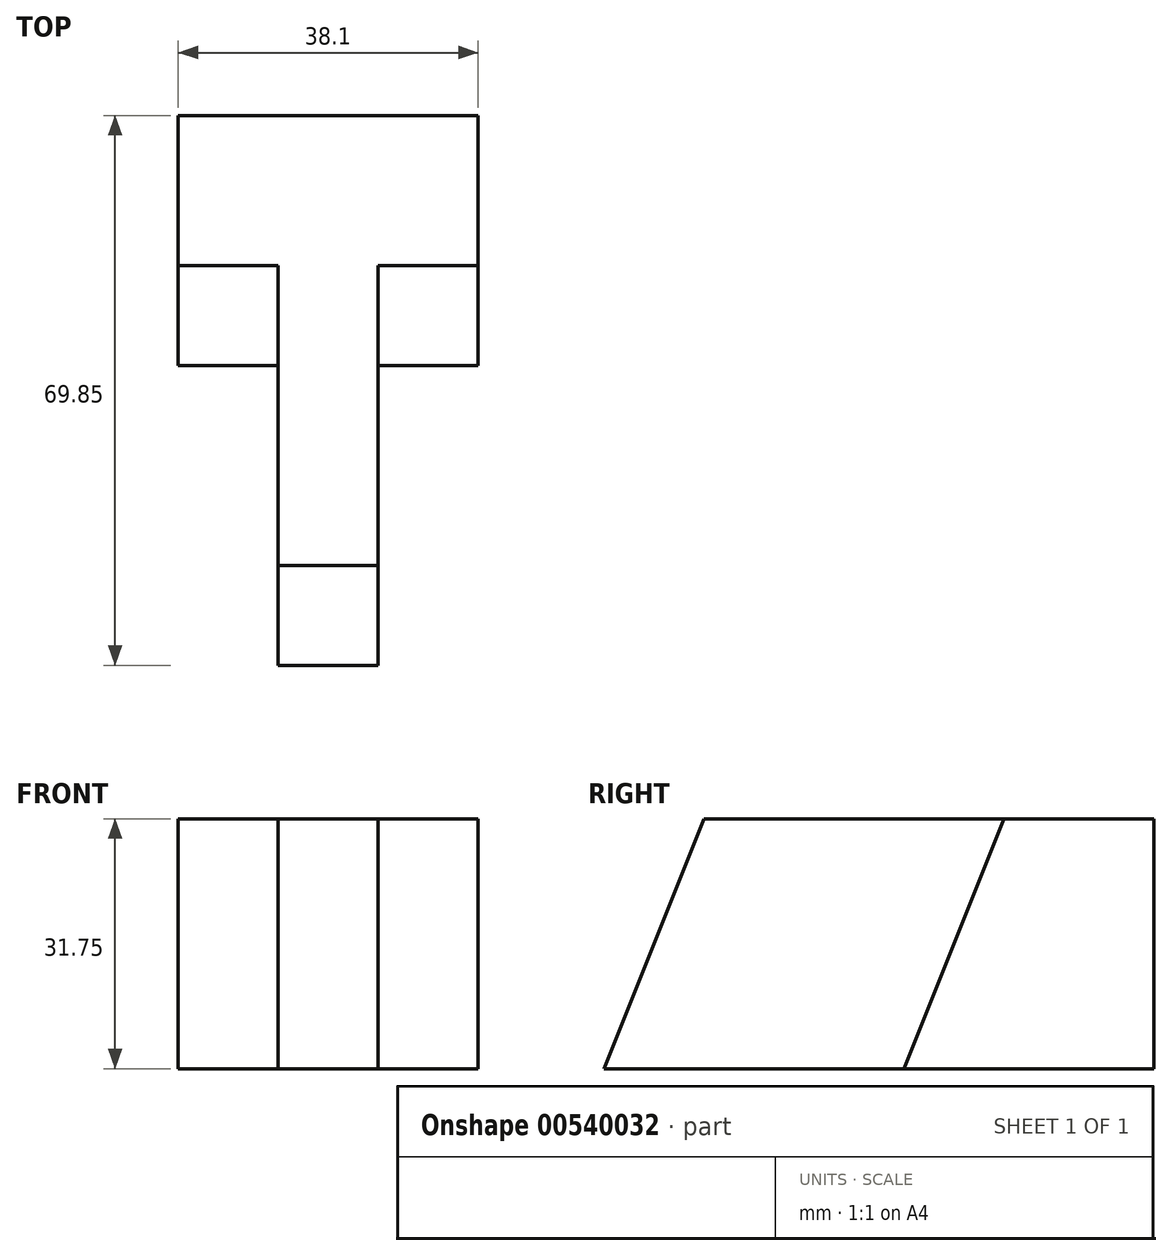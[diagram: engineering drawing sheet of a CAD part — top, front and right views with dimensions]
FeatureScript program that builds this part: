
annotation { "Feature Type Name" : "Feature", "Feature Type Description" : "" }
export const myFeature = defineFeature(function(context is Context, id is Id, definition is map)
    precondition{}
    {
        {
            var Q0;
            Q0=qCreatedBy(makeId("Top.planeOp"),FACE);
            var sketch = newSketch(context, id + "F0", { "sketchPlane" : qUnion([Q0])});
            skLineSegment(sketch, "E0", {"start": v(-15.79, 47.95) * mm, "end": v(22.31, 47.95) * mm});
            skLineSegment(sketch, "E1", {"start": v(22.31, 47.95) * mm, "end": v(22.31, 16.2) * mm});
            skLineSegment(sketch, "E2", {"start": v(22.31, 16.2) * mm, "end": v(9.61, 16.2) * mm});
            skLineSegment(sketch, "E3", {"start": v(9.61, 16.2) * mm, "end": v(9.61, -21.9) * mm});
            skLineSegment(sketch, "E4", {"start": v(9.61, -21.9) * mm, "end": v(-3.09, -21.9) * mm});
            skLineSegment(sketch, "E5", {"start": v(-3.09, -21.9) * mm, "end": v(-3.09, 16.2) * mm});
            skLineSegment(sketch, "E6", {"start": v(-3.09, 16.2) * mm, "end": v(-15.79, 16.2) * mm});
            skLineSegment(sketch, "E7", {"start": v(-15.79, 16.2) * mm, "end": v(-15.79, 47.95) * mm});
            skSolve(sketch);
        }
        {
            var Q0;
            Q0 = qSketchRegion(id + "F0", true);
            extrude(context, id + "F1", {"entities" : qUnion([Q0]), "depth" : 31.75 * mm, "offsetDistance" : 25.4 * mm});
        }
        {
            var Q0;
            Q0=makeQuery(id+"F1.opExtrude","SWEPT_FACE",FACE,{"disambiguationData":[OSD([sQuery(id+"F0.wireOp",EDGE,"E3")])]});
            var sketch = newSketch(context, id + "F2", { "sketchPlane" : qUnion([Q0])});
            skLineSegment(sketch, "E8", {"start": v(-9.2, 31.75) * mm, "end": v(-21.9, 0) * mm});
            skSolve(sketch);
        }
        {
            var Q0;
            {var subQ0=sQuery(id+"F2.wireOp",EDGE,"E8");Q0=makeQuery(id+"F2.imprint","IMPRINT",FACE,{"disambiguationData":[TD([[makeQuery(id+"F2.imprint","IMPRINT",EDGE,{"derivedFrom":subQ0}),-1.0]])]});}
            extrude(context, id + "F3", {"entities" : qUnion([Q0]), "operationType" : NewBodyOperationType.REMOVE, "oppositeDirection" : true, "depth" : 12.7 * mm, "offsetDistance" : 25.4 * mm});
        }
        {
            var Q0;
            Q0=makeQuery(id+"F1.opExtrude","SWEPT_FACE",FACE,{"disambiguationData":[OSD([sQuery(id+"F0.wireOp",EDGE,"E1")])]});
            var sketch = newSketch(context, id + "F4", { "sketchPlane" : qUnion([Q0])});
            skLineSegment(sketch, "E9", {"start": v(28.9, 31.75) * mm, "end": v(16.2, 0) * mm});
            skSolve(sketch);
        }
        {
            var Q0;
            {var subQ0=sQuery(id+"F4.wireOp",EDGE,"E9");Q0=makeQuery(id+"F4.imprint","IMPRINT",FACE,{"disambiguationData":[TD([[makeQuery(id+"F4.imprint","IMPRINT",EDGE,{"derivedFrom":subQ0}),-1.0]])]});}
            extrude(context, id + "F5", {"entities" : qUnion([Q0]), "operationType" : NewBodyOperationType.REMOVE, "oppositeDirection" : true, "depth" : 12.7 * mm, "offsetDistance" : 25.4 * mm});
        }
        {
            var Q0;
            Q0=makeQuery(id+"F1.opExtrude","SWEPT_FACE",FACE,{"disambiguationData":[OSD([sQuery(id+"F0.wireOp",EDGE,"E7")])]});
            var sketch = newSketch(context, id + "F6", { "sketchPlane" : qUnion([Q0])});
            skLineSegment(sketch, "E10", {"start": v(-28.9, 31.75) * mm, "end": v(-16.2, 0) * mm});
            skSolve(sketch);
        }
        {
            var Q0;
            {var subQ0=sQuery(id+"F6.wireOp",EDGE,"E10");Q0=makeQuery(id+"F6.imprint","IMPRINT",FACE,{"disambiguationData":[TD([[makeQuery(id+"F6.imprint","IMPRINT",EDGE,{"derivedFrom":subQ0}),1.0]])]});}
            extrude(context, id + "F7", {"entities" : qUnion([Q0]), "operationType" : NewBodyOperationType.REMOVE, "oppositeDirection" : true, "depth" : 12.7 * mm, "offsetDistance" : 25.4 * mm});
        }
    });
